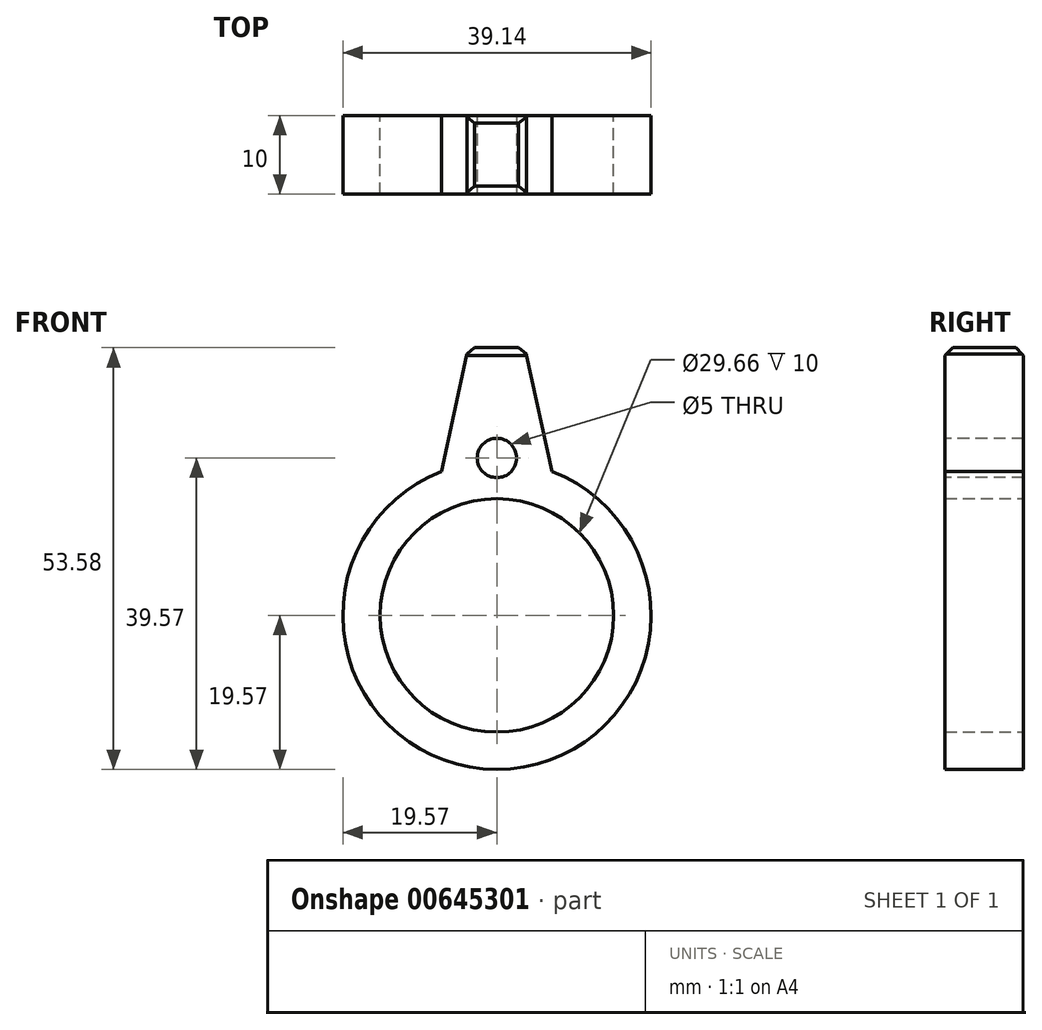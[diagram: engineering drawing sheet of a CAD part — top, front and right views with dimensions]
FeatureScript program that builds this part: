
annotation { "Feature Type Name" : "Feature", "Feature Type Description" : "" }
export const myFeature = defineFeature(function(context is Context, id is Id, definition is map)
    precondition{}
    {
        {
            var Q0;
            Q0=qCreatedBy(makeId("Front.planeOp"),FACE);
            var sketch = newSketch(context, id + "F0", { "sketchPlane" : qUnion([Q0])});
            skCircle(sketch, "E0", {"center": v(0, 0) * mm, "radius": 14.83 * mm});
            skLineSegment(sketch, "E1", {"start": v(0, 42.82) * mm, "end": v(0, -50.87) * mm, "construction": true});
            skLineSegment(sketch, "E2", {"start": v(0, 34) * mm, "end": v(-3.65, 34) * mm});
            skLineSegment(sketch, "E3", {"start": v(-3.65, 34) * mm, "end": v(-7.03, 18.27) * mm});
            skLineSegment(sketch, "E4", {"start": v(0, 34) * mm, "end": v(3.83, 34) * mm});
            skLineSegment(sketch, "E5", {"start": v(3.45, 34.5) * mm, "end": v(7.03, 18.27) * mm});
            skArc(sketch, "E6", {"start": v(7.03, 18.27) * mm, "mid": v(0, -19.57) * mm, "end": v(-7.03, 18.27) * mm});
            skSolve(sketch);
        }
        {
            var Q0;
            Q0 = qSketchRegion(id + "F0", true);
            extrude(context, id + "F1", {"entities" : qUnion([Q0]), "depth" : 10 * mm, "offsetDistance" : 25.4 * mm});
        }
        {
            var Q0;
            Q0=makeQuery(id+"F1.opExtrude","SWEPT_FACE",FACE,{"disambiguationData":[OSD([sQuery(id+"F0.wireOp",EDGE,"E2"),sQuery(id+"F0.wireOp",EDGE,"E4")])]});
            chamfer(context, id + "F2", {"entities" : qUnion([Q0]), "width" : 1 * mm, "tangentPropagation" : true});
        }
        {
            var Q0;
            Q0=makeQuery(id+"F1.opExtrude","CAP_FACE",FACE,{"disambiguationData":[OSD([sQuery(id+"F0.wireOp",EDGE,"E0"),sQuery(id+"F0.wireOp",EDGE,"E2"),sQuery(id+"F0.wireOp",EDGE,"E3"),sQuery(id+"F0.wireOp",EDGE,"E4"),sQuery(id+"F0.wireOp",EDGE,"E5"),sQuery(id+"F0.wireOp",EDGE,"E6")])],"isStart":false});
            var sketch = newSketch(context, id + "F3", { "sketchPlane" : qUnion([Q0])});
            skCircle(sketch, "E7", {"center": v(0, 20) * mm, "radius": 2.5 * mm});
            skSolve(sketch);
        }
        {
            var Q0;
            Q0 = qSketchRegion(id + "F3", true);
            extrude(context, id + "F4", {"entities" : qUnion([Q0]), "operationType" : NewBodyOperationType.REMOVE, "endBound" : BoundingType.THROUGH_ALL, "oppositeDirection" : true, "depth" : 25.4 * mm, "offsetDistance" : 25.4 * mm});
        }
    });
